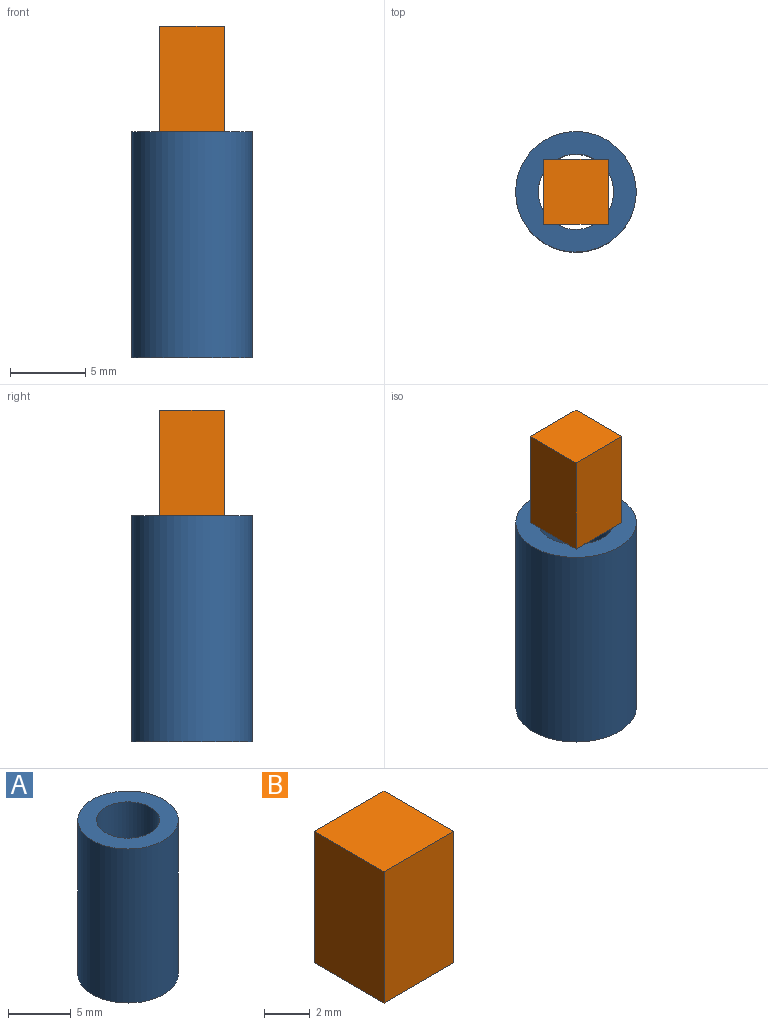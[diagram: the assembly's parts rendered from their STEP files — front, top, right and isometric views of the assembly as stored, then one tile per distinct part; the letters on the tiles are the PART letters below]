
ASSEMBLY  parts=2 mates=1
PART A: 4 faces, bbox 8x8x15 mm
  f0: cylinder r=2.5mm len=15mm, axis (0,0,-1), area 235.6mm2, adj f2,f3
  f1: cylinder r=4mm len=15mm, axis (0,0,-1), area 377mm2, adj f2,f3
  f2: plane 8x8mm, normal (0,0,1), area 30.6mm2, adj f0,f1
  f3: plane 8x8mm, normal (0,0,-1), area 30.6mm2, adj f0,f1
PART B: 6 faces, bbox 4.3x4.3x7 mm
  f0: plane 7x4.3mm, normal (0,-1,0), area 30.1mm2, adj f1,f3,f4,f5
  f1: plane 7x4.3mm, normal (1,0,0), area 30.1mm2, adj f0,f2,f4,f5
  f2: plane 7x4.3mm, normal (0,1,0), area 30.1mm2, adj f1,f3,f4,f5
  f3: plane 7x4.3mm, normal (-1,0,0), area 30.1mm2, adj f0,f2,f4,f5
  f4: plane 4.3x4.3mm, normal (0,0,1), area 18.5mm2, adj f0,f1,f2,f3
  f5: plane 4.3x4.3mm, normal (0,0,-1), area 18.5mm2, adj f0,f1,f2,f3
PLACE A t=(-3.22,-2.28,-8.12)mm
PLACE B rot(axis=(0.71,0.71,0),180deg) t=(-3.22,-2.28,13.88)mm
MATE fastened B.f4 <-> A.f0  axis (0,0,-1) through (-3.22,-2.28,6.88)mm
